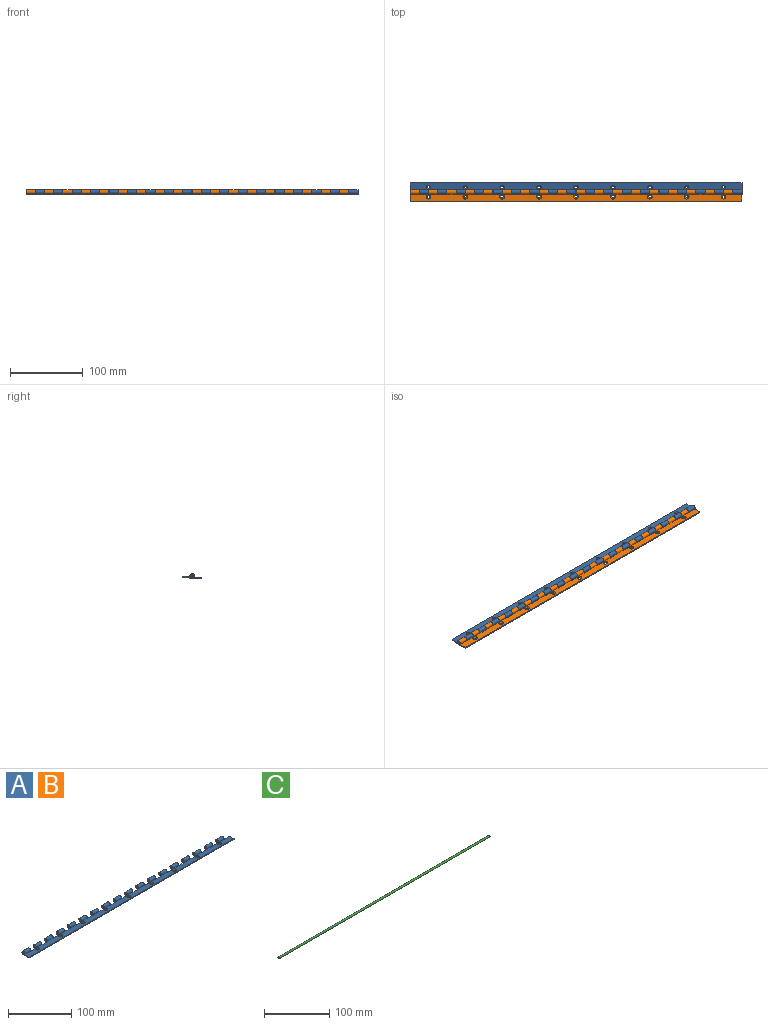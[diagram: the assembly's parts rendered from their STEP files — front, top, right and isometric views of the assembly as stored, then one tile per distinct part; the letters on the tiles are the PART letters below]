
ASSEMBLY  parts=3 mates=2
PART A: 121 faces, bbox 457.2x15.8x6.2 mm
  f0: plane 12.7x1.53mm, normal (0,1,0), area 19.3mm2, adj f1,f35,f36,f79,f120
  f1: plane 6.35x6.22mm, normal (-1,0,0), area 23.7mm2, adj f0,f34,f35,f36,f53,f70,f120
  f2: plane 12.7x1.53mm, normal (0,1,0), area 19.3mm2, adj f3,f35,f36,f83,f119
  f3: plane 6.35x6.22mm, normal (-1,0,0), area 23.7mm2, adj f2,f32,f35,f36,f51,f68,f119
  f4: plane 12.7x1.53mm, normal (0,1,0), area 19.3mm2, adj f5,f35,f36,f87,f118
  f5: plane 6.35x6.22mm, normal (-1,0,0), area 23.7mm2, adj f4,f30,f35,f36,f49,f66,f118
  f6: plane 12.7x1.53mm, normal (0,1,0), area 19.3mm2, adj f7,f35,f36,f91,f117
  f7: plane 6.35x6.22mm, normal (-1,0,0), area 23.7mm2, adj f6,f28,f35,f36,f47,f64,f117
  f8: plane 12.7x1.53mm, normal (0,1,0), area 19.3mm2, adj f9,f35,f36,f95,f116
  f9: plane 6.35x6.22mm, normal (-1,0,0), area 23.7mm2, adj f8,f26,f35,f36,f45,f62,f116
  f10: plane 12.7x1.53mm, normal (0,1,0), area 19.3mm2, adj f11,f35,f36,f99,f115
  f11: plane 6.35x6.22mm, normal (-1,0,0), area 23.7mm2, adj f10,f24,f35,f36,f43,f60,f115
  f12: plane 12.7x1.53mm, normal (0,1,0), area 19.3mm2, adj f13,f35,f36,f103,f114
  f13: plane 6.35x6.22mm, normal (-1,0,0), area 23.7mm2, adj f12,f22,f35,f36,f41,f58,f114
  f14: plane 12.7x1.53mm, normal (0,1,0), area 19.3mm2, adj f15,f35,f36,f107,f113
  f15: plane 6.35x6.22mm, normal (-1,0,0), area 23.7mm2, adj f14,f20,f35,f36,f39,f56,f113
  f16: plane 12.7x1.53mm, normal (0,1,0), area 19.3mm2, adj f17,f35,f36,f111,f112
  f17: plane 6.35x6.22mm, normal (-1,0,0), area 23.7mm2, adj f16,f18,f35,f36,f37,f54,f112
  f18: cylinder r=1.59mm len=12.7mm, axis (-1,0,0), area 105.5mm2, adj f17,f35,f54,f109
  f19: cylinder r=1.59mm len=12.7mm, axis (-1,0,0), area 105.5mm2, adj f35,f55,f107,f110
  f20: cylinder r=1.59mm len=12.7mm, axis (-1,0,0), area 105.5mm2, adj f15,f35,f56,f105
  f21: cylinder r=1.59mm len=12.7mm, axis (-1,0,0), area 105.5mm2, adj f35,f57,f103,f106
  f22: cylinder r=1.59mm len=12.7mm, axis (-1,0,0), area 105.5mm2, adj f13,f35,f58,f101
  f23: cylinder r=1.59mm len=12.7mm, axis (-1,0,0), area 105.5mm2, adj f35,f59,f99,f102
  f24: cylinder r=1.59mm len=12.7mm, axis (-1,0,0), area 105.5mm2, adj f11,f35,f60,f97
  f25: cylinder r=1.59mm len=12.7mm, axis (-1,0,0), area 105.5mm2, adj f35,f61,f95,f98
  f26: cylinder r=1.59mm len=12.7mm, axis (-1,0,0), area 105.5mm2, adj f9,f35,f62,f93
  f27: cylinder r=1.59mm len=12.7mm, axis (-1,0,0), area 105.5mm2, adj f35,f63,f91,f94
  f28: cylinder r=1.59mm len=12.7mm, axis (-1,0,0), area 105.5mm2, adj f7,f35,f64,f89
  f29: cylinder r=1.59mm len=12.7mm, axis (-1,0,0), area 105.5mm2, adj f35,f65,f87,f90
  f30: cylinder r=1.59mm len=12.7mm, axis (-1,0,0), area 105.5mm2, adj f5,f35,f66,f85
  f31: cylinder r=1.59mm len=12.7mm, axis (-1,0,0), area 105.5mm2, adj f35,f67,f83,f86
  f32: cylinder r=1.59mm len=12.7mm, axis (-1,0,0), area 105.5mm2, adj f3,f35,f68,f81
  f33: cylinder r=1.59mm len=12.7mm, axis (-1,0,0), area 105.5mm2, adj f35,f69,f79,f82
  f34: cylinder r=1.59mm len=12.7mm, axis (-1,0,0), area 105.5mm2, adj f1,f35,f70,f77
  f35: plane 457.2x12.7mm, normal (0,0,1), area 4770.3mm2, adj f0,f1,f2,f3,f4,f5,f6,f7
  f36: plane 457.2x12.7mm, normal (0,0,-1), area 4962.6mm2, adj f0,f1,f2,f3,f4,f5,f6,f7
  f37: cylinder r=3.11mm len=12.7mm, axis (-1,0,0), area 206.7mm2, adj f17,f36,f54,f109
  f38: cylinder r=3.11mm len=12.7mm, axis (-1,0,0), area 206.7mm2, adj f36,f55,f107,f110
  f39: cylinder r=3.11mm len=12.7mm, axis (-1,0,0), area 206.7mm2, adj f15,f36,f56,f105
  f40: cylinder r=3.11mm len=12.7mm, axis (-1,0,0), area 206.7mm2, adj f36,f57,f103,f106
  f41: cylinder r=3.11mm len=12.7mm, axis (-1,0,0), area 206.7mm2, adj f13,f36,f58,f101
  f42: cylinder r=3.11mm len=12.7mm, axis (-1,0,0), area 206.7mm2, adj f36,f59,f99,f102
  f43: cylinder r=3.11mm len=12.7mm, axis (-1,0,0), area 206.7mm2, adj f11,f36,f60,f97
  f44: cylinder r=3.11mm len=12.7mm, axis (-1,0,0), area 206.7mm2, adj f36,f61,f95,f98
  f45: cylinder r=3.11mm len=12.7mm, axis (-1,0,0), area 206.7mm2, adj f9,f36,f62,f93
  f46: cylinder r=3.11mm len=12.7mm, axis (-1,0,0), area 206.7mm2, adj f36,f63,f91,f94
  f47: cylinder r=3.11mm len=12.7mm, axis (-1,0,0), area 206.7mm2, adj f7,f36,f64,f89
  f48: cylinder r=3.11mm len=12.7mm, axis (-1,0,0), area 206.7mm2, adj f36,f65,f87,f90
  f49: cylinder r=3.11mm len=12.7mm, axis (-1,0,0), area 206.7mm2, adj f5,f36,f66,f85
  f50: cylinder r=3.11mm len=12.7mm, axis (-1,0,0), area 206.7mm2, adj f36,f67,f83,f86
  f51: cylinder r=3.11mm len=12.7mm, axis (-1,0,0), area 206.7mm2, adj f3,f36,f68,f81
  f52: cylinder r=3.11mm len=12.7mm, axis (-1,0,0), area 206.7mm2, adj f36,f69,f79,f82
  f53: cylinder r=3.11mm len=12.7mm, axis (-1,0,0), area 206.7mm2, adj f1,f36,f70,f77
  f54: plane 12.7x1.32mm, normal (0,0.5,-0.87), area 19.4mm2, adj f17,f18,f37,f109
  f55: plane 12.7x1.32mm, normal (0,0.5,-0.87), area 19.4mm2, adj f19,f38,f107,f110
  f56: plane 12.7x1.32mm, normal (0,0.5,-0.87), area 19.4mm2, adj f15,f20,f39,f105
  f57: plane 12.7x1.32mm, normal (0,0.5,-0.87), area 19.4mm2, adj f21,f40,f103,f106
  f58: plane 12.7x1.32mm, normal (0,0.5,-0.87), area 19.4mm2, adj f13,f22,f41,f101
  f59: plane 12.7x1.32mm, normal (0,0.5,-0.87), area 19.4mm2, adj f23,f42,f99,f102
  f60: plane 12.7x1.32mm, normal (0,0.5,-0.87), area 19.4mm2, adj f11,f24,f43,f97
  f61: plane 12.7x1.32mm, normal (0,0.5,-0.87), area 19.4mm2, adj f25,f44,f95,f98
  f62: plane 12.7x1.32mm, normal (0,0.5,-0.87), area 19.4mm2, adj f9,f26,f45,f93
  f63: plane 12.7x1.32mm, normal (0,0.5,-0.87), area 19.4mm2, adj f27,f46,f91,f94
  f64: plane 12.7x1.32mm, normal (0,0.5,-0.87), area 19.4mm2, adj f7,f28,f47,f89
  f65: plane 12.7x1.32mm, normal (0,0.5,-0.87), area 19.4mm2, adj f29,f48,f87,f90
  f66: plane 12.7x1.32mm, normal (0,0.5,-0.87), area 19.4mm2, adj f5,f30,f49,f85
  f67: plane 12.7x1.32mm, normal (0,0.5,-0.87), area 19.4mm2, adj f31,f50,f83,f86
  f68: plane 12.7x1.32mm, normal (0,0.5,-0.87), area 19.4mm2, adj f3,f32,f51,f81
  f69: plane 12.7x1.32mm, normal (0,0.5,-0.87), area 19.4mm2, adj f33,f52,f79,f82
  f70: plane 12.7x1.32mm, normal (0,0.5,-0.87), area 19.4mm2, adj f1,f34,f53,f77
  f71: plane 9.46x1.52mm, normal (1,0,0), area 14.4mm2, adj f35,f36,f73,f78
  f72: cylinder r=1.59mm len=12.7mm, axis (-1,0,0), area 105.5mm2, adj f35,f75,f76,f111
  f73: plane 457.2x1.52mm, normal (0,-1,0), area 696.8mm2, adj f35,f36,f71,f76
  f74: cylinder r=3.11mm len=12.7mm, axis (-1,0,0), area 206.7mm2, adj f36,f75,f76,f111
  f75: plane 12.7x1.32mm, normal (0,0.5,-0.87), area 19.4mm2, adj f72,f74,f76,f111
  f76: plane 15.81x6.22mm, normal (-1,0,0), area 38.1mm2, adj f35,f36,f72,f73,f74,f75
  f77: plane 6.35x6.22mm, normal (1,0,0), area 23.7mm2, adj f34,f35,f36,f53,f70,f78
  f78: plane 12.7x1.52mm, normal (0,1,0), area 19.4mm2, adj f35,f36,f71,f77
  f79: plane 6.35x6.22mm, normal (1,0,0), area 23.7mm2, adj f0,f33,f35,f36,f52,f69
  f80: plane 12.7x1.52mm, normal (0,1,0), area 19.4mm2, adj f35,f36,f81,f82
  f81: plane 6.35x6.22mm, normal (1,0,0), area 23.7mm2, adj f32,f35,f36,f51,f68,f80
  f82: plane 6.35x6.22mm, normal (-1,0,0), area 23.7mm2, adj f33,f35,f36,f52,f69,f80
  f83: plane 6.35x6.22mm, normal (1,0,0), area 23.7mm2, adj f2,f31,f35,f36,f50,f67
  f84: plane 12.7x1.52mm, normal (0,1,0), area 19.4mm2, adj f35,f36,f85,f86
  f85: plane 6.35x6.22mm, normal (1,0,0), area 23.7mm2, adj f30,f35,f36,f49,f66,f84
  f86: plane 6.35x6.22mm, normal (-1,0,0), area 23.7mm2, adj f31,f35,f36,f50,f67,f84
  f87: plane 6.35x6.22mm, normal (1,0,0), area 23.7mm2, adj f4,f29,f35,f36,f48,f65
  f88: plane 12.7x1.52mm, normal (0,1,0), area 19.4mm2, adj f35,f36,f89,f90
  f89: plane 6.35x6.22mm, normal (1,0,0), area 23.7mm2, adj f28,f35,f36,f47,f64,f88
  f90: plane 6.35x6.22mm, normal (-1,0,0), area 23.7mm2, adj f29,f35,f36,f48,f65,f88
  f91: plane 6.35x6.22mm, normal (1,0,0), area 23.7mm2, adj f6,f27,f35,f36,f46,f63
  f92: plane 12.7x1.52mm, normal (0,1,0), area 19.4mm2, adj f35,f36,f93,f94
  f93: plane 6.35x6.22mm, normal (1,0,0), area 23.7mm2, adj f26,f35,f36,f45,f62,f92
  f94: plane 6.35x6.22mm, normal (-1,0,0), area 23.7mm2, adj f27,f35,f36,f46,f63,f92
  f95: plane 6.35x6.22mm, normal (1,0,0), area 23.7mm2, adj f8,f25,f35,f36,f44,f61
  f96: plane 12.7x1.52mm, normal (0,1,0), area 19.4mm2, adj f35,f36,f97,f98
  f97: plane 6.35x6.22mm, normal (1,0,0), area 23.7mm2, adj f24,f35,f36,f43,f60,f96
  f98: plane 6.35x6.22mm, normal (-1,0,0), area 23.7mm2, adj f25,f35,f36,f44,f61,f96
  f99: plane 6.35x6.22mm, normal (1,0,0), area 23.7mm2, adj f10,f23,f35,f36,f42,f59
  f100: plane 12.7x1.52mm, normal (0,1,0), area 19.4mm2, adj f35,f36,f101,f102
  f101: plane 6.35x6.22mm, normal (1,0,0), area 23.7mm2, adj f22,f35,f36,f41,f58,f100
  f102: plane 6.35x6.22mm, normal (-1,0,0), area 23.7mm2, adj f23,f35,f36,f42,f59,f100
  f103: plane 6.35x6.22mm, normal (1,0,0), area 23.7mm2, adj f12,f21,f35,f36,f40,f57
  f104: plane 12.7x1.52mm, normal (0,1,0), area 19.4mm2, adj f35,f36,f105,f106
  f105: plane 6.35x6.22mm, normal (1,0,0), area 23.7mm2, adj f20,f35,f36,f39,f56,f104
  f106: plane 6.35x6.22mm, normal (-1,0,0), area 23.7mm2, adj f21,f35,f36,f40,f57,f104
  f107: plane 6.35x6.22mm, normal (1,0,0), area 23.7mm2, adj f14,f19,f35,f36,f38,f55
  f108: plane 12.7x1.52mm, normal (0,1,0), area 19.4mm2, adj f35,f36,f109,f110
  f109: plane 6.35x6.22mm, normal (1,0,0), area 23.7mm2, adj f18,f35,f36,f37,f54,f108
  f110: plane 6.35x6.22mm, normal (-1,0,0), area 23.7mm2, adj f19,f35,f36,f38,f55,f108
  f111: plane 6.35x6.22mm, normal (1,0,0), area 23.7mm2, adj f16,f35,f36,f72,f74,f75
  f112: cone r=1.47mm half-angle=41deg, axis (0,0,1), area 32.6mm2, adj f16,f17,f35,f36
  f113: cone r=1.47mm half-angle=41deg, axis (0,0,1), area 32.6mm2, adj f14,f15,f35,f36
  f114: cone r=1.47mm half-angle=41deg, axis (0,0,1), area 32.6mm2, adj f12,f13,f35,f36
  f115: cone r=1.47mm half-angle=41deg, axis (0,0,1), area 32.6mm2, adj f10,f11,f35,f36
  f116: cone r=1.47mm half-angle=41deg, axis (0,0,1), area 32.6mm2, adj f8,f9,f35,f36
  f117: cone r=1.47mm half-angle=41deg, axis (0,0,1), area 32.6mm2, adj f6,f7,f35,f36
  f118: cone r=1.47mm half-angle=41deg, axis (0,0,1), area 32.6mm2, adj f4,f5,f35,f36
  f119: cone r=1.47mm half-angle=41deg, axis (0,0,1), area 32.6mm2, adj f2,f3,f35,f36
  f120: cone r=1.47mm half-angle=41deg, axis (0,0,1), area 32.6mm2, adj f0,f1,f35,f36
PART B: same geometry as A
PART C: 3 faces, bbox 457.2x3.2x3.2 mm
  f0: plane 3.18x3.18mm, normal (1,0,0), area 7.9mm2, adj f1
  f1: cylinder r=1.59mm len=457.2mm, axis (-1,0,0), area 4560.4mm2, adj f0,f2
  f2: plane 3.18x3.18mm, normal (-1,0,0), area 7.9mm2, adj f1
PLACE A rot(axis=(0,-0.04,1),180deg) t=(457.2,0,0)mm
PLACE B at identity
PLACE C at identity
MATE revolute B.f18 <-> C.f1  axis (-1,0,0) through (0,0,0)mm
MATE revolute A.f18 <-> C.f1  axis (1,0,0) through (457.2,0,0)mm
